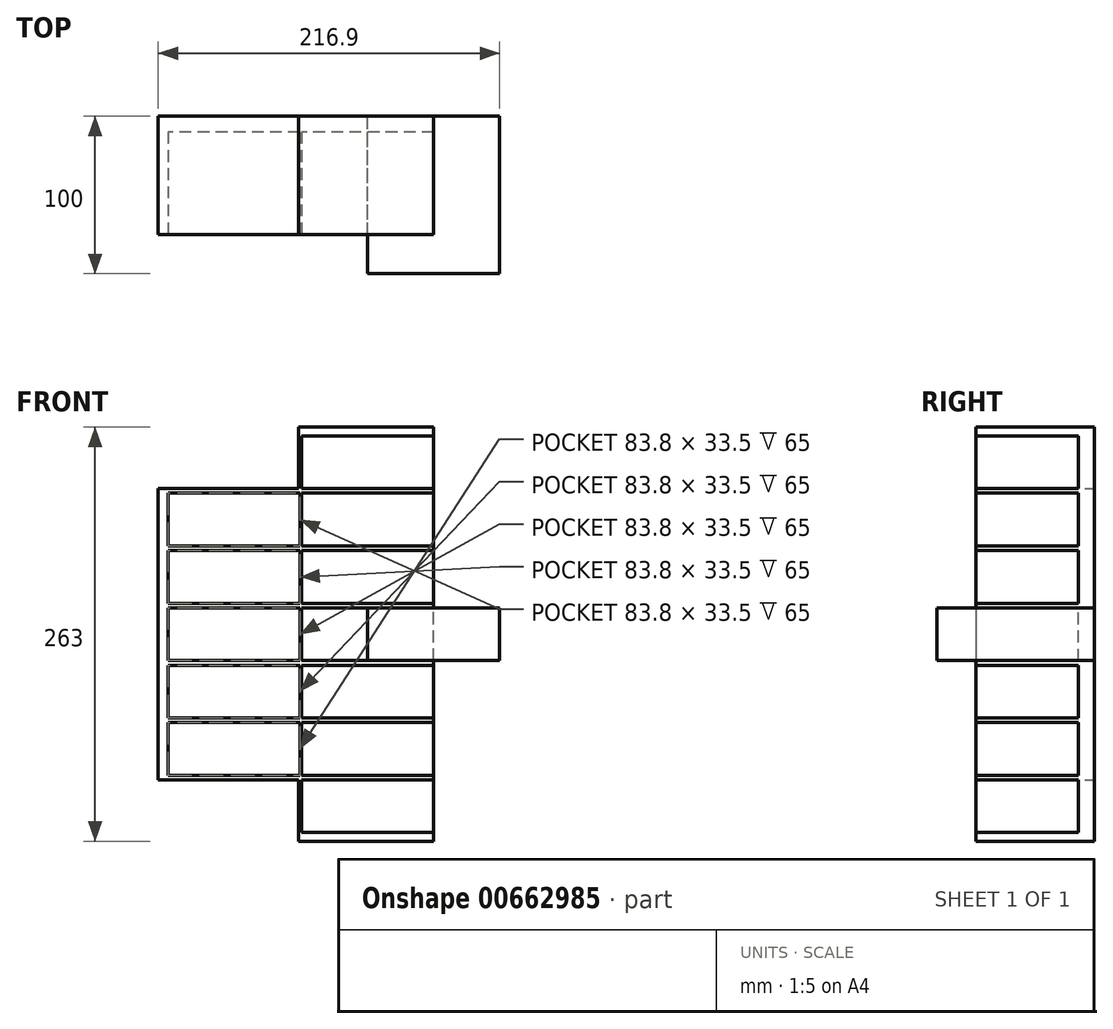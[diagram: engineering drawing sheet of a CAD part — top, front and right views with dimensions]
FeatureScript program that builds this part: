
annotation { "Feature Type Name" : "Feature", "Feature Type Description" : "" }
export const myFeature = defineFeature(function(context is Context, id is Id, definition is map)
    precondition{}
    {
        {
            var Q0;
            Q0=qCreatedBy(makeId("Front.planeOp"),FACE);
            var sketch = newSketch(context, id + "F0", { "sketchPlane" : qUnion([Q0])});
            skLineSegment(sketch, "E0", {"start": v(0, 131.5) * mm, "end": v(-86, 131.5) * mm});
            skLineSegment(sketch, "E1", {"start": v(-86, 131.5) * mm, "end": v(-86, 92.5) * mm});
            skLineSegment(sketch, "E2", {"start": v(-86, 92.5) * mm, "end": v(-175, 92.5) * mm});
            skLineSegment(sketch, "E3", {"start": v(-175, 92.5) * mm, "end": v(-175, 0) * mm});
            skLineSegment(sketch, "E4", {"start": v(-175, 0) * mm, "end": v(-175, -92.5) * mm});
            skLineSegment(sketch, "E5", {"start": v(-175, -92.5) * mm, "end": v(-86, -92.5) * mm});
            skLineSegment(sketch, "E6", {"start": v(-86, -92.5) * mm, "end": v(-86, -131.5) * mm});
            skLineSegment(sketch, "E7", {"start": v(-86, -131.5) * mm, "end": v(0, -131.5) * mm});
            skLineSegment(sketch, "E8", {"start": v(0, -131.5) * mm, "end": v(0, 0) * mm});
            skLineSegment(sketch, "E9", {"start": v(0, 0) * mm, "end": v(0, 131.5) * mm});
            skSolve(sketch);
        }
        {
            var Q0;
            Q0=makeQuery(id+"F0.imprint","IMPRINT",FACE,{"disambiguationData":[TD([[makeQuery(id+"F0.imprint","IMPRINT",EDGE,{"derivedFrom":sQuery(id+"F0.wireOp",EDGE,"E0")}),1.0]])]});
            extrude(context, id + "F1", {"entities" : qUnion([Q0]), "depth" : 75 * mm, "offsetDistance" : 25 * mm});
        }
        {
            var Q0;
            Q0=makeQuery(id+"F1.opExtrude","CAP_FACE",FACE,{"disambiguationData":[OSD([sQuery(id+"F0.wireOp",EDGE,"E0"),sQuery(id+"F0.wireOp",EDGE,"E1"),sQuery(id+"F0.wireOp",EDGE,"E2"),sQuery(id+"F0.wireOp",EDGE,"E3"),sQuery(id+"F0.wireOp",EDGE,"E4"),sQuery(id+"F0.wireOp",EDGE,"E5"),sQuery(id+"F0.wireOp",EDGE,"E6"),sQuery(id+"F0.wireOp",EDGE,"E7"),sQuery(id+"F0.wireOp",EDGE,"E8"),sQuery(id+"F0.wireOp",EDGE,"E9")])],"isStart":false});
            var sketch = newSketch(context, id + "F2", { "sketchPlane" : qUnion([Q0])});
            skLineSegment(sketch, "E10.bottom", {"start": v(0, 16.75) * mm, "end": v(-83.8, 16.75) * mm});
            skLineSegment(sketch, "E10.top", {"start": v(0, -16.75) * mm, "end": v(-83.8, -16.75) * mm});
            skLineSegment(sketch, "E10.left", {"start": v(0, 16.75) * mm, "end": v(0, -16.75) * mm});
            skLineSegment(sketch, "E10.right", {"start": v(-83.8, 16.75) * mm, "end": v(-83.8, -16.75) * mm});
            skLineSegment(sketch, "E11.bottom", {"start": v(0, 19.67) * mm, "end": v(-83.8, 19.67) * mm});
            skLineSegment(sketch, "E11.top", {"start": v(0, 53.17) * mm, "end": v(-83.8, 53.17) * mm});
            skLineSegment(sketch, "E11.left", {"start": v(0, 19.67) * mm, "end": v(0, 53.17) * mm});
            skLineSegment(sketch, "E11.right", {"start": v(-83.8, 19.67) * mm, "end": v(-83.8, 53.17) * mm});
            skLineSegment(sketch, "E12.bottom", {"start": v(0, 56.1) * mm, "end": v(-83.8, 56.1) * mm});
            skLineSegment(sketch, "E12.top", {"start": v(0, 89.6) * mm, "end": v(-83.8, 89.6) * mm});
            skLineSegment(sketch, "E12.left", {"start": v(0, 56.1) * mm, "end": v(0, 89.6) * mm});
            skLineSegment(sketch, "E12.right", {"start": v(-83.8, 56.1) * mm, "end": v(-83.8, 89.6) * mm});
            skLineSegment(sketch, "E13.bottom", {"start": v(0, 92.52) * mm, "end": v(-83.8, 92.52) * mm});
            skLineSegment(sketch, "E13.top", {"start": v(0, 126.02) * mm, "end": v(-83.8, 126.02) * mm});
            skLineSegment(sketch, "E13.left", {"start": v(0, 92.52) * mm, "end": v(0, 126.02) * mm});
            skLineSegment(sketch, "E13.right", {"start": v(-83.8, 92.52) * mm, "end": v(-83.8, 126.02) * mm});
            skLineSegment(sketch, "E14", {"start": v(-83.8, 92.52) * mm, "end": v(-83.8, 89.6) * mm, "construction": true});
            skLineSegment(sketch, "E15", {"start": v(-83.8, 56.1) * mm, "end": v(-83.8, 53.17) * mm, "construction": true});
            skLineSegment(sketch, "E16", {"start": v(-83.8, 19.67) * mm, "end": v(-83.8, 16.75) * mm, "construction": true});
            skLineSegment(sketch, "E17.bottom", {"start": v(0, -19.67) * mm, "end": v(-83.8, -19.67) * mm});
            skLineSegment(sketch, "E17.top", {"start": v(0, -53.17) * mm, "end": v(-83.8, -53.17) * mm});
            skLineSegment(sketch, "E17.left", {"start": v(0, -19.67) * mm, "end": v(0, -53.17) * mm});
            skLineSegment(sketch, "E17.right", {"start": v(-83.8, -19.67) * mm, "end": v(-83.8, -53.17) * mm});
            skLineSegment(sketch, "E18.bottom", {"start": v(0, -56.1) * mm, "end": v(-83.8, -56.1) * mm});
            skLineSegment(sketch, "E18.top", {"start": v(0, -89.6) * mm, "end": v(-83.8, -89.6) * mm});
            skLineSegment(sketch, "E18.left", {"start": v(0, -56.1) * mm, "end": v(0, -89.6) * mm});
            skLineSegment(sketch, "E18.right", {"start": v(-83.8, -56.1) * mm, "end": v(-83.8, -89.6) * mm});
            skLineSegment(sketch, "E19.bottom", {"start": v(0, -92.52) * mm, "end": v(-83.8, -92.52) * mm});
            skLineSegment(sketch, "E19.top", {"start": v(0, -126.02) * mm, "end": v(-83.8, -126.02) * mm});
            skLineSegment(sketch, "E19.left", {"start": v(0, -92.52) * mm, "end": v(0, -126.02) * mm});
            skLineSegment(sketch, "E19.right", {"start": v(-83.8, -92.52) * mm, "end": v(-83.8, -126.02) * mm});
            skLineSegment(sketch, "E20", {"start": v(-83.8, -56.1) * mm, "end": v(-83.8, -53.17) * mm, "construction": true});
            skLineSegment(sketch, "E21", {"start": v(-83.8, -92.52) * mm, "end": v(-83.8, -89.6) * mm, "construction": true});
            skLineSegment(sketch, "E22", {"start": v(-83.8, -19.67) * mm, "end": v(-83.8, -16.75) * mm, "construction": true});
            skLineSegment(sketch, "E23.bottom", {"start": v(-85, 56.1) * mm, "end": v(-168.8, 56.1) * mm});
            skLineSegment(sketch, "E23.top", {"start": v(-85, 89.6) * mm, "end": v(-168.8, 89.6) * mm});
            skLineSegment(sketch, "E23.left", {"start": v(-85, 56.1) * mm, "end": v(-85, 89.6) * mm});
            skLineSegment(sketch, "E23.right", {"start": v(-168.8, 56.1) * mm, "end": v(-168.8, 89.6) * mm});
            skLineSegment(sketch, "E24.bottom", {"start": v(-85, 53.17) * mm, "end": v(-168.8, 53.17) * mm});
            skLineSegment(sketch, "E24.top", {"start": v(-85, 19.67) * mm, "end": v(-168.8, 19.67) * mm});
            skLineSegment(sketch, "E24.left", {"start": v(-85, 53.17) * mm, "end": v(-85, 19.67) * mm});
            skLineSegment(sketch, "E24.right", {"start": v(-168.8, 53.17) * mm, "end": v(-168.8, 19.67) * mm});
            skLineSegment(sketch, "E25.bottom", {"start": v(-85, 16.75) * mm, "end": v(-168.8, 16.75) * mm});
            skLineSegment(sketch, "E25.top", {"start": v(-85, -16.75) * mm, "end": v(-168.8, -16.75) * mm});
            skLineSegment(sketch, "E25.left", {"start": v(-85, 16.75) * mm, "end": v(-85, -16.75) * mm});
            skLineSegment(sketch, "E25.right", {"start": v(-168.8, 16.75) * mm, "end": v(-168.8, -16.75) * mm});
            skLineSegment(sketch, "E26.bottom", {"start": v(-85, -19.67) * mm, "end": v(-168.8, -19.67) * mm});
            skLineSegment(sketch, "E26.top", {"start": v(-85, -53.17) * mm, "end": v(-168.8, -53.17) * mm});
            skLineSegment(sketch, "E26.left", {"start": v(-85, -19.67) * mm, "end": v(-85, -53.17) * mm});
            skLineSegment(sketch, "E26.right", {"start": v(-168.8, -19.67) * mm, "end": v(-168.8, -53.17) * mm});
            skLineSegment(sketch, "E27.bottom", {"start": v(-85, -56.1) * mm, "end": v(-168.8, -56.1) * mm});
            skLineSegment(sketch, "E27.top", {"start": v(-85, -89.6) * mm, "end": v(-168.8, -89.6) * mm});
            skLineSegment(sketch, "E27.left", {"start": v(-85, -56.1) * mm, "end": v(-85, -89.6) * mm});
            skLineSegment(sketch, "E27.right", {"start": v(-168.8, -56.1) * mm, "end": v(-168.8, -89.6) * mm});
            skSolve(sketch);
        }
        {
            var Q0;
            Q0=makeQuery(id+"F2.imprint","IMPRINT",FACE,{"disambiguationData":[TD([[makeQuery(id+"F2.imprint","IMPRINT",EDGE,{"derivedFrom":sQuery(id+"F2.wireOp",EDGE,"E13.bottom")}),-1.0]])]});
            var Q1;
            Q1=makeQuery(id+"F2.imprint","IMPRINT",FACE,{"disambiguationData":[TD([[makeQuery(id+"F2.imprint","IMPRINT",EDGE,{"derivedFrom":sQuery(id+"F2.wireOp",EDGE,"E23.bottom")}),-1.0]])]});
            var Q2;
            Q2=makeQuery(id+"F2.imprint","IMPRINT",FACE,{"disambiguationData":[TD([[makeQuery(id+"F2.imprint","IMPRINT",EDGE,{"derivedFrom":sQuery(id+"F2.wireOp",EDGE,"E12.bottom")}),-1.0]])]});
            var Q3;
            Q3=makeQuery(id+"F2.imprint","IMPRINT",FACE,{"disambiguationData":[TD([[makeQuery(id+"F2.imprint","IMPRINT",EDGE,{"derivedFrom":sQuery(id+"F2.wireOp",EDGE,"E24.bottom")}),1.0]])]});
            var Q4;
            Q4=makeQuery(id+"F2.imprint","IMPRINT",FACE,{"disambiguationData":[TD([[makeQuery(id+"F2.imprint","IMPRINT",EDGE,{"derivedFrom":sQuery(id+"F2.wireOp",EDGE,"E11.bottom")}),-1.0]])]});
            var Q5;
            Q5=makeQuery(id+"F2.imprint","IMPRINT",FACE,{"disambiguationData":[TD([[makeQuery(id+"F2.imprint","IMPRINT",EDGE,{"derivedFrom":sQuery(id+"F2.wireOp",EDGE,"E25.bottom")}),1.0]])]});
            var Q6;
            Q6=makeQuery(id+"F2.imprint","IMPRINT",FACE,{"disambiguationData":[TD([[makeQuery(id+"F2.imprint","IMPRINT",EDGE,{"derivedFrom":sQuery(id+"F2.wireOp",EDGE,"E10.bottom")}),1.0]])]});
            var Q7;
            Q7=makeQuery(id+"F2.imprint","IMPRINT",FACE,{"disambiguationData":[TD([[makeQuery(id+"F2.imprint","IMPRINT",EDGE,{"derivedFrom":sQuery(id+"F2.wireOp",EDGE,"E26.bottom")}),1.0]])]});
            var Q8;
            Q8=makeQuery(id+"F2.imprint","IMPRINT",FACE,{"disambiguationData":[TD([[makeQuery(id+"F2.imprint","IMPRINT",EDGE,{"derivedFrom":sQuery(id+"F2.wireOp",EDGE,"E17.bottom")}),1.0]])]});
            var Q9;
            Q9=makeQuery(id+"F2.imprint","IMPRINT",FACE,{"disambiguationData":[TD([[makeQuery(id+"F2.imprint","IMPRINT",EDGE,{"derivedFrom":sQuery(id+"F2.wireOp",EDGE,"E27.bottom")}),1.0]])]});
            var Q10;
            Q10=makeQuery(id+"F2.imprint","IMPRINT",FACE,{"disambiguationData":[TD([[makeQuery(id+"F2.imprint","IMPRINT",EDGE,{"derivedFrom":sQuery(id+"F2.wireOp",EDGE,"E18.bottom")}),1.0]])]});
            var Q11;
            Q11=makeQuery(id+"F2.imprint","IMPRINT",FACE,{"disambiguationData":[TD([[makeQuery(id+"F2.imprint","IMPRINT",EDGE,{"derivedFrom":sQuery(id+"F2.wireOp",EDGE,"E19.bottom")}),1.0]])]});
            extrude(context, id + "F3", {"entities" : qUnion([Q0, Q1, Q2, Q3, Q4, Q5, Q6, Q7, Q8, Q9, Q10, Q11]), "operationType" : NewBodyOperationType.REMOVE, "oppositeDirection" : true, "depth" : 65 * mm, "offsetDistance" : 25 * mm});
        }
        {
            var Q0;
            Q0=qCreatedBy(makeId("Front.planeOp"),FACE);
            var sketch = newSketch(context, id + "F4", { "sketchPlane" : qUnion([Q0])});
            skLineSegment(sketch, "E28.bottom", {"start": v(41.9, -16.75) * mm, "end": v(-41.9, -16.75) * mm});
            skLineSegment(sketch, "E28.top", {"start": v(41.9, 16.75) * mm, "end": v(-41.9, 16.75) * mm});
            skLineSegment(sketch, "E28.left", {"start": v(41.9, -16.75) * mm, "end": v(41.9, 16.75) * mm});
            skLineSegment(sketch, "E28.right", {"start": v(-41.9, -16.75) * mm, "end": v(-41.9, 16.75) * mm});
            skPoint(sketch, "E28.middle", {"position": v(0, 0) * mm});
            skSolve(sketch);
        }
        {
            var Q0;
            Q0=makeQuery(id+"F4.imprint","IMPRINT",FACE,{"disambiguationData":[TD([[makeQuery(id+"F4.imprint","IMPRINT",EDGE,{"derivedFrom":sQuery(id+"F4.wireOp",EDGE,"E28.bottom")}),-1.0]])]});
            extrude(context, id + "F5", {"entities" : qUnion([Q0]), "depth" : 100 * mm, "offsetDistance" : 25 * mm});
        }
        {
            var Q0;
            Q0=makeQuery(id+"F4.imprint","IMPRINT",FACE,{"disambiguationData":[TD([[makeQuery(id+"F4.imprint","IMPRINT",EDGE,{"derivedFrom":sQuery(id+"F4.wireOp",EDGE,"E28.bottom")}),-1.0]])]});
            extrude(context, id + "F6", {"entities" : qUnion([Q0]), "depth" : 100 * mm, "offsetDistance" : 25 * mm});
        }
    });
